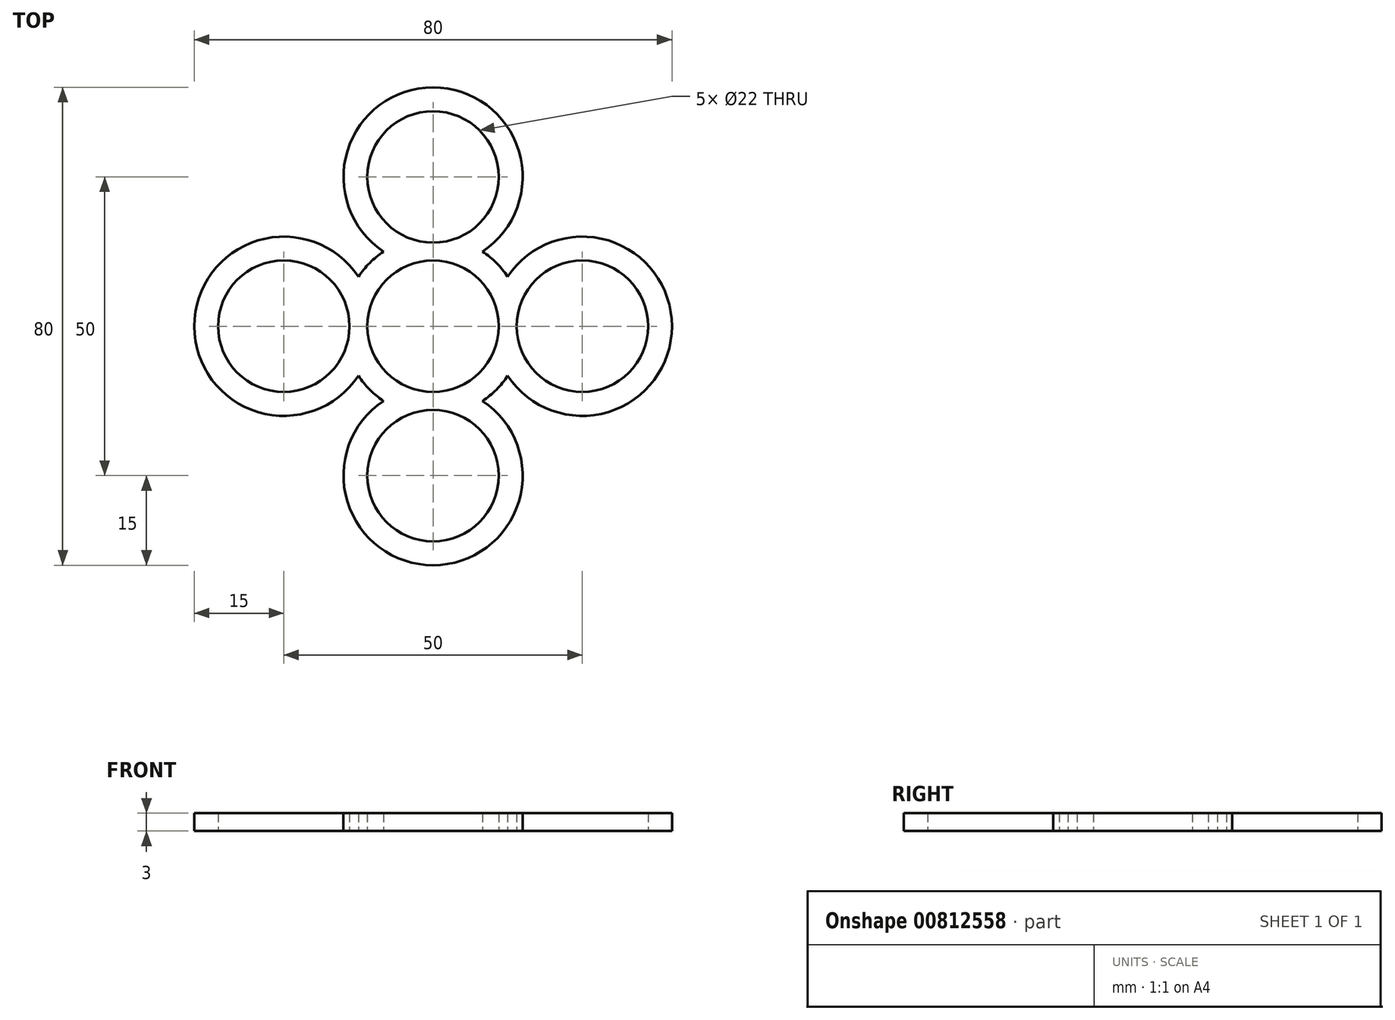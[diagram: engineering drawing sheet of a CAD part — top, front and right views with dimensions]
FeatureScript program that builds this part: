
annotation { "Feature Type Name" : "Feature", "Feature Type Description" : "" }
export const myFeature = defineFeature(function(context is Context, id is Id, definition is map)
    precondition{}
    {
        {
            var Q0;
            Q0=qCreatedBy(makeId("Top.planeOp"),FACE);
            var sketch = newSketch(context, id + "F0", { "sketchPlane" : qUnion([Q0])});
            skArc(sketch, "E0", {"start": v(7.78, 7.78) * mm, "mid": v(0, 11) * mm, "end": v(-7.78, 7.78) * mm});
            skArc(sketch, "E1", {"start": v(-8.3, 12.5) * mm, "mid": v(-9.5, 11.61) * mm, "end": v(-10.6, 10.6) * mm});
            skCircle(sketch, "E2", {"center": v(0, 25) * mm, "radius": 11 * mm});
            skArc(sketch, "E3", {"start": v(8.3, 12.5) * mm, "mid": v(0, 40) * mm, "end": v(-8.3, 12.5) * mm});
            skArc(sketch, "E4.trimOffspring", {"start": v(10.6, 10.6) * mm, "mid": v(9.5, 11.61) * mm, "end": v(8.3, 12.5) * mm});
            skArc(sketch, "E5.1.0", {"start": v(-12.5, 8.3) * mm, "mid": v(-40, 0) * mm, "end": v(-12.5, -8.3) * mm});
            skCircle(sketch, "E5.1.1", {"center": v(-25, 0) * mm, "radius": 11 * mm});
            skArc(sketch, "E5.1.2", {"start": v(-10.6, 10.6) * mm, "mid": v(-11.61, 9.5) * mm, "end": v(-12.5, 8.3) * mm});
            skArc(sketch, "E5.1.3", {"start": v(-7.78, 7.78) * mm, "mid": v(-11, 0) * mm, "end": v(-7.78, -7.78) * mm});
            skArc(sketch, "E5.1.4", {"start": v(-12.5, -8.3) * mm, "mid": v(-11.61, -9.5) * mm, "end": v(-10.6, -10.6) * mm});
            skArc(sketch, "E5.2.0", {"start": v(-8.3, -12.5) * mm, "mid": v(0, -40) * mm, "end": v(8.3, -12.5) * mm});
            skCircle(sketch, "E5.2.1", {"center": v(0, -25) * mm, "radius": 11 * mm});
            skArc(sketch, "E5.2.2", {"start": v(-10.6, -10.6) * mm, "mid": v(-9.5, -11.61) * mm, "end": v(-8.3, -12.5) * mm});
            skArc(sketch, "E5.2.3", {"start": v(-7.78, -7.78) * mm, "mid": v(0, -11) * mm, "end": v(7.78, -7.78) * mm});
            skArc(sketch, "E5.2.4", {"start": v(8.3, -12.5) * mm, "mid": v(9.5, -11.61) * mm, "end": v(10.6, -10.6) * mm});
            skArc(sketch, "E5.3.0", {"start": v(12.5, -8.3) * mm, "mid": v(40, 0) * mm, "end": v(12.5, 8.3) * mm});
            skCircle(sketch, "E5.3.1", {"center": v(25, 0) * mm, "radius": 11 * mm});
            skArc(sketch, "E5.3.2", {"start": v(10.6, -10.6) * mm, "mid": v(11.61, -9.5) * mm, "end": v(12.5, -8.3) * mm});
            skArc(sketch, "E5.3.3", {"start": v(7.78, -7.78) * mm, "mid": v(11, 0) * mm, "end": v(7.78, 7.78) * mm});
            skArc(sketch, "E5.3.4", {"start": v(12.5, 8.3) * mm, "mid": v(11.61, 9.5) * mm, "end": v(10.6, 10.6) * mm});
            skSolve(sketch);
        }
        {
            var Q0;
            Q0 = qSketchRegion(id + "F0", true);
            extrude(context, id + "F1", {"entities" : qUnion([Q0]), "depth" : 3 * mm, "offsetDistance" : 25 * mm});
        }
    });
